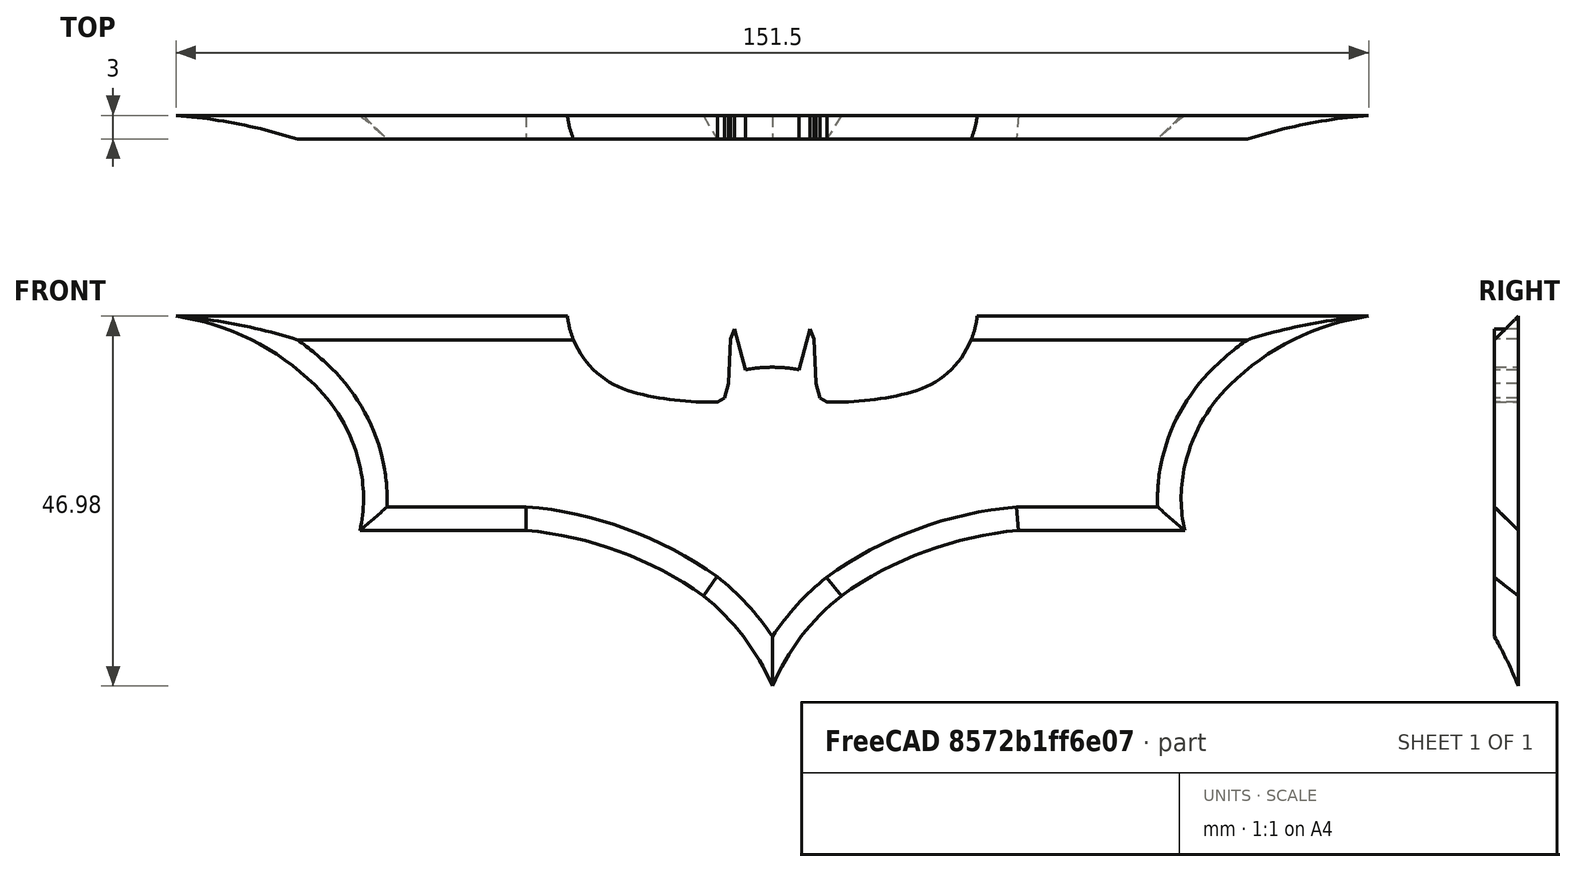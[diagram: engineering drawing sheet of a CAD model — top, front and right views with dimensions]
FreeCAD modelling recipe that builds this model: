
FCSTD DOCUMENT  (FreeCAD 0.17R13541 (Git))
Label: 蝙蝠镖
License: All rights reserved
LicenseURL: http://en.wikipedia.org/wiki/All_rights_reserved
objects: Image::ImagePlane×1, Sketcher::SketchObject×1, PartDesign::Pad×1, PartDesign::Mirrored×1, PartDesign::Chamfer×1, PartDesign::Body×1
note: 6 computed .brp shape members not serialized (recipe doc carries the construction recipe); baked Part::Feature solids carry a one-line shape summary decoded from their .brp

FEATURE [Image::ImagePlane] ImagePlane
  Placement = pos=(0,0,0) rot=(-1,0,0;4.71239rad)
  XSize = 184.239
  YSize = 116.666
FEATURE [Sketcher::SketchObject] Sketch
  MapMode = 5
  Placement = pos=(0,0,0) rot=(1,0,0;1.5708rad)
  Support = -> [XZ_Plane]
  sketch-geometry (16):
    g0: LineSegment StartX=0 StartY=11.3 StartZ=0 EndX=0 EndY=-29.2 EndZ=0
    g1: ArcOfCircle CenterX=27.2239 CenterY=-40.9378 CenterZ=0 NormalX=0 NormalY=0 NormalZ=1 AngleXU=0 Radius=29.6465 StartAngle=2.24281 EndAngle=2.73452
    g2: ArcOfCircle CenterX=35.2482 CenterY=-54.8551 CenterZ=0 NormalX=0 NormalY=0 NormalZ=1 AngleXU=0 Radius=45.5958 StartAngle=1.65769 EndAngle=2.19049
    g3: LineSegment StartX=31.2911 StartY=-9.4313 StartZ=0 EndX=52.3824 EndY=-9.4313 EndZ=0
    g4: ArcOfCircle CenterX=70.6185 CenterY=-5.35259 CenterZ=0 NormalX=0 NormalY=0 NormalZ=1 AngleXU=0 Radius=18.6866 StartAngle=2.94197 EndAngle=3.36163
    g5: ArcOfCircle CenterX=72.5937 CenterY=-5.75222 CenterZ=0 NormalX=0 NormalY=0 NormalZ=1 AngleXU=0 Radius=20.7019 StartAngle=2.34649 EndAngle=2.94197
    g6: ArcOfCircle CenterX=80.3286 CenterY=-13.6387 CenterZ=0 NormalX=0 NormalY=0 NormalZ=1 AngleXU=0 Radius=31.7484 StartAngle=1.71565 EndAngle=2.34649
    g7: LineSegment StartX=75.7458 StartY=17.7772 StartZ=0 EndX=26.0233 EndY=17.7772 EndZ=0
    g8: ArcOfCircle CenterX=14.8087 CenterY=19.0488 CenterZ=0 NormalX=0 NormalY=0 NormalZ=1 AngleXU=0 Radius=11.2865 StartAngle=4.97659 EndAngle=6.17028
    g9: ArcOfCircle CenterX=8.09165 CenterY=43.8788 CenterZ=0 NormalX=0 NormalY=0 NormalZ=1 AngleXU=0 Radius=37.009 StartAngle=4.68124 EndAngle=4.97659
    g10: LineSegment StartX=6.93908 StartY=6.88775 StartZ=0 EndX=6.05163 EndY=7.36077 EndZ=0
    g11: LineSegment StartX=6.05163 StartY=7.36077 StartZ=0 EndX=5.54004 EndY=9.23661 EndZ=0
    g12: LineSegment StartX=5.54004 StartY=9.23661 StartZ=0 EndX=5.28424 EndY=14.8642 EndZ=0
    g13: LineSegment StartX=5.28424 StartY=14.8642 StartZ=0 EndX=4.80107 EndY=16.1431 EndZ=0
    g14: LineSegment StartX=4.80107 StartY=16.1431 StartZ=0 EndX=3.37997 EndY=10.9704 EndZ=0
    g15: ArcOfCircle CenterX=0 CenterY=-6.19279 CenterZ=0 NormalX=0 NormalY=0 NormalZ=1 AngleXU=0 Radius=17.4928 StartAngle=1.37635 EndAngle=1.5708
  constraints (24):
    c: Vertical(g0)
    c: DistanceX(g0) = 0
    c: DistanceY(g0) = 11.3
    c: DistanceY(g0,g0) = 40.5
    c: Coincident(g1,g0)
    c: Coincident(g2,g1)
    c: Coincident(g3,g2)
    c: Horizontal(g3)
    c: Coincident(g4,g3)
    c: PointOnObject(g5,g4)
    c: Tangent(g6,g5) = -1.5708
    c: Tangent(g5,g4) = -1.5708
    c: Coincident(g7,g6)
    c: Horizontal(g7)
    c: Coincident(g8,g7)
    c: Tangent(g9,g8) = -1.5708
    c: Coincident(g10,g9)
    c: Coincident(g10,g11)
    c: Coincident(g11,g12)
    c: Coincident(g12,g13)
    c: Coincident(g13,g14)
    c: Coincident(g15,g14)
    c: Coincident(g15,g0)
    c: Perpendicular(g15,g0)
FEATURE [PartDesign::Pad] Pad
  Length = 3
  Length2 = 100
  Placement = pos=(0,0,0) rot=(1,0,0;1.5708rad)
  Profile = -> Sketch
  Type = 0
FEATURE [PartDesign::Mirrored] Mirrored
  BaseFeature = -> Pad
  MirrorPlane = -> YZ_Plane
  Originals = -> [Pad]
  Placement = pos=(0,0,0) rot=(1,0,0;1.5708rad)
  Refine = true
FEATURE [PartDesign::Chamfer] Chamfer
  Base = -> Mirrored [Edge65,Edge63,Edge54,Edge68,Edge77,Edge85]
  BaseFeature = -> Mirrored
  Placement = pos=(0,0,0) rot=(1,0,0;1.5708rad)
  Size = 2.999
FEATURE [PartDesign::Body] Body
  Group = -> [Sketch,Pad,Mirrored,Chamfer]
  Origin = -> Origin
  Tip = -> Chamfer
